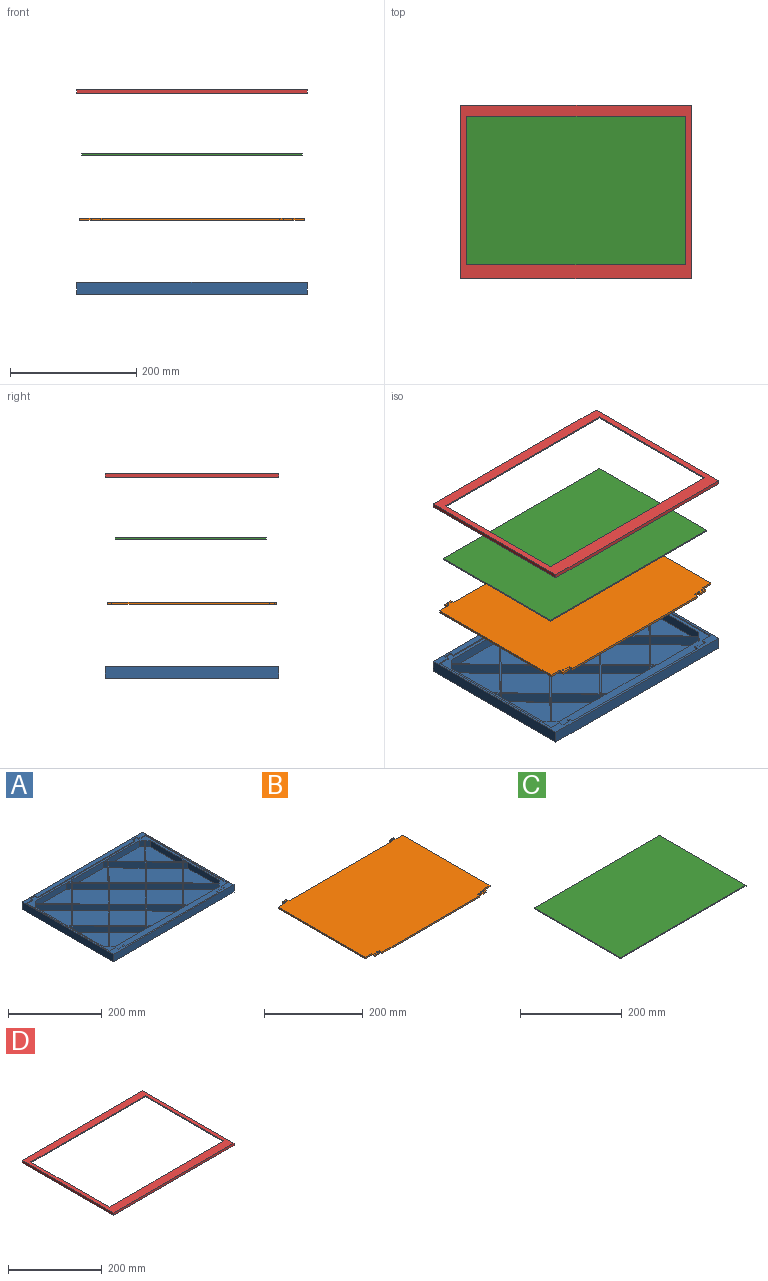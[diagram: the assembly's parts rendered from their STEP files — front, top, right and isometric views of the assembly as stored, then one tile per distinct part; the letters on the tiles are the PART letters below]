
ASSEMBLY  parts=4 mates=4
PART A: 150 faces, bbox 365x275x19 mm
  f0: plane 365x19mm, normal (0,-1,0), area 6935mm2, adj f1,f3,f4,f29
  f1: plane 275x19mm, normal (1,0,0), area 5225mm2, adj f0,f2,f4,f29
  f2: plane 365x19mm, normal (0,1,0), area 6935mm2, adj f1,f3,f4,f29
  f3: plane 275x19mm, normal (-1,0,0), area 5225mm2, adj f0,f2,f4,f29
  f4: plane 365x275mm, normal (0,0,-1), area 100375mm2, adj f0,f1,f2,f3
  f5: plane 7x2mm, normal (-1,0,0), area 14mm2, adj f6,f28,f29,f30
  f6: plane 19x2mm, normal (0,-1,0), area 38mm2, adj f5,f7,f29,f30
  f7: plane 250x2mm, normal (-1,0,0), area 500mm2, adj f6,f8,f29,f30
  f8: plane 19x2mm, normal (0,1,0), area 38mm2, adj f7,f9,f29,f30
  f9: plane 8x2mm, normal (-1,0,0), area 16mm2, adj f8,f10,f29,f30
  f10: plane 15x2mm, normal (0,1,0), area 30mm2, adj f9,f11,f29,f30
  f11: plane 4x2mm, normal (1,0,0), area 8mm2, adj f10,f12,f29,f30
  f12: plane 6x2mm, normal (0,1,0), area 12mm2, adj f11,f13,f29,f30
  f13: plane 7x2mm, normal (-1,0,0), area 14mm2, adj f12,f14,f29,f30
  f14: plane 281x2mm, normal (0,1,0), area 562mm2, adj f13,f15,f29,f30
  f15: plane 7x2mm, normal (1,0,0), area 14mm2, adj f14,f16,f29,f30
  f16: plane 3x2mm, normal (0,1,0), area 6mm2, adj f15,f17,f29,f30
  f17: plane 4x2mm, normal (-1,0,0), area 8mm2, adj f16,f18,f29,f30
  f18: plane 15x2mm, normal (0,1,0), area 30mm2, adj f17,f19,f29,f30
  f19: plane 8x2mm, normal (1,0,0), area 16mm2, adj f18,f20,f29,f30
  f20: plane 19x2mm, normal (0,1,0), area 38mm2, adj f19,f21,f29,f30
  f21: plane 250x2mm, normal (1,0,0), area 500mm2, adj f20,f22,f29,f30
  f22: plane 19x2mm, normal (0,-1,0), area 38mm2, adj f21,f23,f29,f30
  f23: plane 7x2mm, normal (1,0,0), area 14mm2, adj f22,f24,f29,f30
  f24: plane 13x2mm, normal (0,-1,0), area 26mm2, adj f23,f25,f29,f30
  f25: plane 7x2mm, normal (-1,0,0), area 14mm2, adj f24,f26,f29,f30
  f26: plane 294x2mm, normal (0,-1,0), area 588mm2, adj f25,f27,f29,f30
  f27: plane 7x2mm, normal (1,0,0), area 14mm2, adj f26,f28,f29,f30
  f28: plane 13x2mm, normal (0,-1,0), area 26mm2, adj f5,f27,f29,f30
  f29: plane 365x275mm, normal (0,0,1), area 7326mm2, adj f0,f1,f2,f3,f5,f6,f7,f8
  f30: plane 358x268mm, normal (0,0,1), area 14181.1mm2, adj f5,f6,f7,f8,f9,f10,f11,f12
  f31: plane 54.85x54.05mm, normal (0.71,-0.7,0), area 1232.1mm2, adj f30,f32,f126,f143
  f32: plane 54.85x54.05mm, normal (-0.71,-0.7,0), area 1232.1mm2, adj f30,f31,f33,f143
  f33: plane 54.85x54.05mm, normal (-0.71,0.7,0), area 1232.1mm2, adj f30,f32,f126,f143
  f34: plane 55.07x54.26mm, normal (0.71,0.7,0), area 1237mm2, adj f30,f35,f104,f142
  f35: plane 54.85x54.05mm, normal (0.71,-0.7,0), area 1232.1mm2, adj f30,f34,f36,f142
  f36: plane 55.07x54.26mm, normal (-0.71,-0.7,0), area 1237mm2, adj f30,f35,f104,f142
  f37: plane 54.85x54.05mm, normal (0.71,0.7,0), area 1232.1mm2, adj f30,f38,f105,f141
  f38: plane 55.07x54.26mm, normal (0.71,-0.7,0), area 1237mm2, adj f30,f37,f39,f141
  f39: plane 54.85x54.05mm, normal (-0.71,-0.7,0), area 1232.1mm2, adj f30,f38,f105,f141
  f40: plane 55.07x54.26mm, normal (0.71,0.7,0), area 1237mm2, adj f30,f41,f106,f140
  f41: plane 55.07x54.26mm, normal (0.71,-0.7,0), area 1237mm2, adj f30,f40,f42,f140
  f42: plane 55.07x54.26mm, normal (-0.71,-0.7,0), area 1237mm2, adj f30,f41,f106,f140
  f43: plane 55.07x54.26mm, normal (0.71,0.7,0), area 1237mm2, adj f30,f44,f107,f139
  f44: plane 54.85x54.05mm, normal (0.71,-0.7,0), area 1232.1mm2, adj f30,f43,f45,f139
  f45: plane 55.07x54.26mm, normal (-0.71,-0.7,0), area 1237mm2, adj f30,f44,f107,f139
  f46: plane 54.85x54.05mm, normal (0.71,0.7,0), area 1232.1mm2, adj f30,f47,f108,f138
  f47: plane 55.07x54.26mm, normal (0.71,-0.7,0), area 1237mm2, adj f30,f46,f48,f138
  f48: plane 54.85x54.05mm, normal (-0.71,-0.7,0), area 1232.1mm2, adj f30,f47,f108,f138
  f49: plane 54.85x54.05mm, normal (0.71,-0.7,0), area 1232.1mm2, adj f30,f50,f109,f137
  f50: plane 54.85x54.05mm, normal (-0.71,-0.7,0), area 1232.1mm2, adj f30,f49,f51,f137
  f51: plane 54.85x54.05mm, normal (-0.71,0.7,0), area 1232.1mm2, adj f30,f50,f109,f137
  f52: plane 16x7.05mm, normal (0.71,-0.7,0), area 158.5mm2, adj f30,f53,f110,f136
  f53: plane 94.2x16mm, normal (0,-1,0), area 1507.1mm2, adj f30,f52,f54,f136
  f54: plane 16x7.05mm, normal (-0.71,-0.7,0), area 158.5mm2, adj f30,f53,f55,f136
  f55: plane 54.85x54.05mm, normal (-0.71,0.7,0), area 1232.1mm2, adj f30,f54,f110,f136
  f56: plane 6x5.63mm, normal (0.71,0.7,0), area 47.4mm2, adj f30,f57,f111,f144
  f57: plane 11.09x6mm, normal (0,-1,0), area 66.6mm2, adj f30,f56,f111,f144
  f58: plane 16x7.36mm, normal (0.71,-0.7,0), area 165.2mm2, adj f30,f59,f112,f135
  f59: plane 94.03x16mm, normal (0,-1,0), area 1504.4mm2, adj f30,f58,f60,f135
  f60: plane 16x7.14mm, normal (-0.71,-0.7,0), area 160.4mm2, adj f30,f59,f61,f135
  f61: plane 55.07x54.26mm, normal (-0.71,0.7,0), area 1237mm2, adj f30,f60,f112,f135
  f62: plane 94.97x16mm, normal (1,0,0), area 1519.6mm2, adj f30,f63,f113,f134
  f63: plane 16x7.37mm, normal (0.71,-0.7,0), area 165.5mm2, adj f30,f62,f64,f134
  f64: plane 54.85x54.05mm, normal (-0.71,-0.7,0), area 1232.1mm2, adj f30,f63,f65,f134
  f65: plane 54.85x54.05mm, normal (-0.71,0.7,0), area 1232.1mm2, adj f30,f64,f113,f134
  f66: plane 11.88x6mm, normal (1,0,0), area 71.3mm2, adj f30,f67,f114,f148
  f67: plane 6x5.94mm, normal (-0.71,-0.7,0), area 50.1mm2, adj f30,f66,f114,f148
  f68: plane 94.97x16mm, normal (1,0,0), area 1519.6mm2, adj f30,f69,f115,f133
  f69: plane 16x7.37mm, normal (0.71,-0.7,0), area 165.5mm2, adj f30,f68,f70,f133
  f70: plane 54.85x54.05mm, normal (-0.71,-0.7,0), area 1232.1mm2, adj f30,f69,f71,f133
  f71: plane 54.85x54.05mm, normal (-0.71,0.7,0), area 1232.1mm2, adj f30,f70,f115,f133
  f72: plane 94.03x16mm, normal (0,1,0), area 1504.4mm2, adj f30,f73,f116,f132
  f73: plane 16x7.36mm, normal (0.71,0.7,0), area 165.2mm2, adj f30,f72,f74,f132
  f74: plane 54.85x54.05mm, normal (0.71,-0.7,0), area 1232.1mm2, adj f30,f73,f75,f132
  f75: plane 55.07x54.26mm, normal (-0.71,-0.7,0), area 1237mm2, adj f30,f74,f116,f132
  f76: plane 11.09x6mm, normal (0,1,0), area 66.6mm2, adj f30,f77,f117,f147
  f77: plane 6x5.63mm, normal (0.71,-0.7,0), area 47.4mm2, adj f30,f76,f117,f147
  f78: plane 94.2x16mm, normal (0,1,0), area 1507.1mm2, adj f30,f79,f118,f131
  f79: plane 16x7.05mm, normal (0.71,0.7,0), area 158.5mm2, adj f30,f78,f80,f131
  f80: plane 54.85x54.05mm, normal (0.71,-0.7,0), area 1232.1mm2, adj f30,f79,f81,f131
  f81: plane 54.85x54.05mm, normal (-0.71,-0.7,0), area 1232.1mm2, adj f30,f80,f118,f131
  f82: plane 11.09x6mm, normal (0,1,0), area 66.6mm2, adj f30,f83,f119,f146
  f83: plane 6x5.63mm, normal (0.71,-0.7,0), area 47.4mm2, adj f30,f82,f119,f146
  f84: plane 94.03x16mm, normal (0,1,0), area 1504.4mm2, adj f30,f85,f120,f130
  f85: plane 16x7.14mm, normal (0.71,0.7,0), area 160.4mm2, adj f30,f84,f86,f130
  f86: plane 55.07x54.26mm, normal (0.71,-0.7,0), area 1237mm2, adj f30,f85,f87,f130
  f87: plane 54.85x54.05mm, normal (-0.71,-0.7,0), area 1232.1mm2, adj f30,f86,f120,f130
  f88: plane 11.09x6mm, normal (0,-1,0), area 66.6mm2, adj f30,f89,f121,f145
  f89: plane 6x5.63mm, normal (-0.71,0.7,0), area 47.4mm2, adj f30,f88,f121,f145
  f90: plane 16x7.37mm, normal (-0.71,-0.7,0), area 165.5mm2, adj f30,f91,f122,f129
  f91: plane 94.97x16mm, normal (-1,0,0), area 1519.6mm2, adj f30,f90,f92,f129
  f92: plane 16x7.37mm, normal (-0.71,0.7,0), area 165.5mm2, adj f30,f91,f93,f129
  f93: plane 54.85x54.05mm, normal (0.71,0.7,0), area 1232.1mm2, adj f30,f92,f122,f129
  f94: plane 6x5.94mm, normal (0.71,-0.7,0), area 50.1mm2, adj f30,f95,f123,f149
  f95: plane 11.88x6mm, normal (-1,0,0), area 71.3mm2, adj f30,f94,f123,f149
  f96: plane 16x7.37mm, normal (-0.71,-0.7,0), area 165.5mm2, adj f30,f97,f124,f128
  f97: plane 94.97x16mm, normal (-1,0,0), area 1519.6mm2, adj f30,f96,f98,f128
  f98: plane 16x7.37mm, normal (-0.71,0.7,0), area 165.5mm2, adj f30,f97,f99,f128
  f99: plane 54.85x54.05mm, normal (0.71,0.7,0), area 1232.1mm2, adj f30,f98,f124,f128
  f100: plane 16x7.14mm, normal (0.71,-0.7,0), area 160.4mm2, adj f30,f101,f125,f127
  f101: plane 94.03x16mm, normal (0,-1,0), area 1504.4mm2, adj f30,f100,f102,f127
  f102: plane 16x7.36mm, normal (-0.71,-0.7,0), area 165.2mm2, adj f30,f101,f103,f127
  f103: plane 54.85x54.05mm, normal (-0.71,0.7,0), area 1232.1mm2, adj f30,f102,f125,f127
  f104: plane 54.85x54.05mm, normal (-0.71,0.7,0), area 1232.1mm2, adj f30,f34,f36,f142
  f105: plane 55.07x54.26mm, normal (-0.71,0.7,0), area 1237mm2, adj f30,f37,f39,f141
  f106: plane 55.07x54.26mm, normal (-0.71,0.7,0), area 1237mm2, adj f30,f40,f42,f140
  f107: plane 54.85x54.05mm, normal (-0.71,0.7,0), area 1232.1mm2, adj f30,f43,f45,f139
  f108: plane 55.07x54.26mm, normal (-0.71,0.7,0), area 1237mm2, adj f30,f46,f48,f138
  f109: plane 54.85x54.05mm, normal (0.71,0.7,0), area 1232.1mm2, adj f30,f49,f51,f137
  f110: plane 54.85x54.05mm, normal (0.71,0.7,0), area 1232.1mm2, adj f30,f52,f55,f136
  f111: plane 6x5.63mm, normal (-0.71,0.7,0), area 47.4mm2, adj f30,f56,f57,f144
  f112: plane 54.85x54.05mm, normal (0.71,0.7,0), area 1232.1mm2, adj f30,f58,f61,f135
  f113: plane 16x7.37mm, normal (0.71,0.7,0), area 165.5mm2, adj f30,f62,f65,f134
  f114: plane 6x5.94mm, normal (-0.71,0.7,0), area 50.1mm2, adj f30,f66,f67,f148
  f115: plane 16x7.37mm, normal (0.71,0.7,0), area 165.5mm2, adj f30,f68,f71,f133
  f116: plane 16x7.14mm, normal (-0.71,0.7,0), area 160.4mm2, adj f30,f72,f75,f132
  f117: plane 6x5.63mm, normal (-0.71,-0.7,0), area 47.4mm2, adj f30,f76,f77,f147
  f118: plane 16x7.05mm, normal (-0.71,0.7,0), area 158.5mm2, adj f30,f78,f81,f131
  f119: plane 6x5.63mm, normal (-0.71,-0.7,0), area 47.4mm2, adj f30,f82,f83,f146
  f120: plane 16x7.36mm, normal (-0.71,0.7,0), area 165.2mm2, adj f30,f84,f87,f130
  f121: plane 6x5.63mm, normal (0.71,0.7,0), area 47.4mm2, adj f30,f88,f89,f145
  f122: plane 54.85x54.05mm, normal (0.71,-0.7,0), area 1232.1mm2, adj f30,f90,f93,f129
  f123: plane 6x5.94mm, normal (0.71,0.7,0), area 50.1mm2, adj f30,f94,f95,f149
  f124: plane 54.85x54.05mm, normal (0.71,-0.7,0), area 1232.1mm2, adj f30,f96,f99,f128
  f125: plane 55.07x54.26mm, normal (0.71,0.7,0), area 1237mm2, adj f30,f100,f103,f127
  f126: plane 54.85x54.05mm, normal (0.71,0.7,0), area 1232.1mm2, adj f30,f31,f33,f143
  f127: plane 108.31x62.21mm, normal (0,0,1), area 3709.7mm2, adj f100,f101,f102,f103,f125
  f128: plane 109.71x61.31mm, normal (0,0,1), area 3707.7mm2, adj f96,f97,f98,f99,f124
  f129: plane 109.71x61.31mm, normal (0,0,1), area 3707.7mm2, adj f90,f91,f92,f93,f122
  f130: plane 108.31x62.21mm, normal (0,0,1), area 3709.7mm2, adj f84,f85,f86,f87,f120
  f131: plane 108.1x61.91mm, normal (0,0,1), area 3678.4mm2, adj f78,f79,f80,f81,f118
  f132: plane 108.31x62.21mm, normal (0,0,1), area 3709.7mm2, adj f72,f73,f74,f75,f116
  f133: plane 109.71x61.31mm, normal (0,0,1), area 3707.7mm2, adj f68,f69,f70,f71,f115
  f134: plane 109.71x61.31mm, normal (0,0,1), area 3707.7mm2, adj f62,f63,f64,f65,f113
  f135: plane 108.31x62.21mm, normal (0,0,1), area 3709.7mm2, adj f58,f59,f60,f61,f112
  f136: plane 108.1x61.91mm, normal (0,0,1), area 3678.4mm2, adj f52,f53,f54,f55,f110
  f137: plane 109.71x108.1mm, normal (0,0,1), area 5929.6mm2, adj f49,f50,f51,f109
  f138: plane 109.92x108.31mm, normal (0,0,1), area 5952.9mm2, adj f46,f47,f48,f108
  f139: plane 109.92x108.31mm, normal (0,0,1), area 5952.9mm2, adj f43,f44,f45,f107
  f140: plane 110.14x108.52mm, normal (0,0,1), area 5976.2mm2, adj f40,f41,f42,f106
  f141: plane 109.92x108.31mm, normal (0,0,1), area 5952.9mm2, adj f37,f38,f39,f105
  f142: plane 109.92x108.31mm, normal (0,0,1), area 5952.9mm2, adj f34,f35,f36,f104
  f143: plane 109.71x108.1mm, normal (0,0,1), area 5929.6mm2, adj f31,f32,f33,f126
  f144: plane 11.09x5.63mm, normal (0,0,1), area 31.2mm2, adj f56,f57,f111
  f145: plane 11.09x5.63mm, normal (0,0,1), area 31.2mm2, adj f88,f89,f121
  f146: plane 11.09x5.63mm, normal (0,0,1), area 31.2mm2, adj f82,f83,f119
  f147: plane 11.09x5.63mm, normal (0,0,1), area 31.2mm2, adj f76,f77,f117
  f148: plane 11.88x5.86mm, normal (0,0,1), area 34.8mm2, adj f66,f67,f114
  f149: plane 11.88x5.86mm, normal (0,0,1), area 34.8mm2, adj f94,f95,f123
PART B: 34 faces, bbox 358x268x3.5 mm
  f0: plane 7x3.5mm, normal (1,0,0), area 24.5mm2, adj f1,f30,f32,f33
  f1: plane 6x3.5mm, normal (0,-1,0), area 21mm2, adj f0,f2,f32,f33
  f2: plane 4x3.5mm, normal (-1,0,0), area 14mm2, adj f1,f3,f32,f33
  f3: plane 15x3.5mm, normal (0,-1,0), area 52.5mm2, adj f2,f4,f32,f33
  f4: plane 8x3.5mm, normal (1,0,0), area 28mm2, adj f3,f5,f32,f33
  f5: plane 19x3.5mm, normal (0,-1,0), area 66.5mm2, adj f4,f6,f32,f33
  f6: plane 250x3.5mm, normal (1,0,0), area 875mm2, adj f5,f7,f32,f33
  f7: plane 19x3.5mm, normal (0,1,0), area 66.5mm2, adj f6,f8,f32,f33
  f8: plane 7x3.5mm, normal (1,0,0), area 24.5mm2, adj f7,f9,f32,f33
  f9: plane 13x3.5mm, normal (0,1,0), area 45.5mm2, adj f8,f10,f32,f33
  f10: plane 7x3.5mm, normal (-1,0,0), area 24.5mm2, adj f9,f11,f32,f33
  f11: plane 294x3.5mm, normal (0,1,0), area 1029mm2, adj f10,f12,f32,f33
  f12: plane 7x3.5mm, normal (1,0,0), area 24.5mm2, adj f11,f13,f32,f33
  f13: plane 13x3.5mm, normal (0,1,0), area 45.5mm2, adj f12,f14,f32,f33
  f14: plane 7x3.5mm, normal (-1,0,0), area 24.5mm2, adj f13,f15,f32,f33
  f15: plane 19x3.5mm, normal (0,1,0), area 66.5mm2, adj f14,f16,f32,f33
  f16: plane 250x3.5mm, normal (-1,0,0), area 875mm2, adj f15,f17,f32,f33
  f17: plane 19x3.5mm, normal (0,-1,0), area 66.5mm2, adj f16,f18,f32,f33
  f18: plane 8x3.5mm, normal (-1,0,0), area 28mm2, adj f17,f19,f32,f33
  f19: plane 15x3.5mm, normal (0,-1,0), area 52.5mm2, adj f18,f20,f32,f33
  f20: plane 4x3.5mm, normal (1,0,0), area 14mm2, adj f19,f21,f32,f33
  f21: plane 3.5x3mm, normal (0,-1,0), area 10.5mm2, adj f20,f22,f32,f33
  f22: plane 7x3.5mm, normal (-1,0,0), area 24.5mm2, adj f21,f30,f32,f33
  f23: cylinder r=1mm len=3.5mm, axis (0,0,-1), area 22mm2, adj f32,f33
  f24: cylinder r=1mm len=3.5mm, axis (0,0,-1), area 22mm2, adj f32,f33
  f25: cylinder r=1mm len=3.5mm, axis (0,0,-1), area 22mm2, adj f32,f33
  f26: cylinder r=1mm len=3.5mm, axis (0,0,-1), area 22mm2, adj f32,f33
  f27: cylinder r=1mm len=3.5mm, axis (0,0,-1), area 22mm2, adj f32,f33
  f28: cylinder r=1mm len=3.5mm, axis (0,0,-1), area 22mm2, adj f32,f33
  f29: cylinder r=1mm len=3.5mm, axis (0,0,-1), area 22mm2, adj f32,f33
  f30: plane 281x3.5mm, normal (0,-1,0), area 983.5mm2, adj f0,f22,f32,f33
  f31: cylinder r=1mm len=3.5mm, axis (0,0,-1), area 22mm2, adj f32,f33
  f32: plane 358x268mm, normal (0,0,1), area 93023.9mm2, adj f0,f1,f2,f3,f4,f5,f6,f7
  f33: plane 358x268mm, normal (0,0,-1), area 93023.9mm2, adj f0,f1,f2,f3,f4,f5,f6,f7
PART C: 6 faces, bbox 350x240x2 mm
  f0: plane 240x2mm, normal (1,0,0), area 480mm2, adj f1,f3,f4,f5
  f1: plane 350x2mm, normal (0,1,0), area 700mm2, adj f0,f2,f4,f5
  f2: plane 240x2mm, normal (-1,0,0), area 480mm2, adj f1,f3,f4,f5
  f3: plane 350x2mm, normal (0,-1,0), area 700mm2, adj f0,f2,f4,f5
  f4: plane 350x240mm, normal (0,0,1), area 84000mm2, adj f0,f1,f2,f3
  f5: plane 350x240mm, normal (0,0,-1), area 84000mm2, adj f0,f1,f2,f3
PART D: 40 faces, bbox 365x275x6 mm
  f0: plane 275x6mm, normal (-1,0,0), area 1650mm2, adj f1,f27,f28,f38
  f1: plane 365x6mm, normal (0,-1,0), area 2190mm2, adj f0,f2,f28,f38
  f2: plane 275x6mm, normal (1,0,0), area 1650mm2, adj f1,f27,f28,f38
  f3: plane 7x2mm, normal (-1,0,0), area 14mm2, adj f4,f26,f28,f33
  f4: plane 19x2mm, normal (0,-1,0), area 38mm2, adj f3,f5,f28,f33
  f5: plane 250x2mm, normal (-1,0,0), area 500mm2, adj f4,f6,f28,f33
  f6: plane 19x2mm, normal (0,1,0), area 38mm2, adj f5,f7,f28,f33
  f7: plane 8x2mm, normal (-1,0,0), area 16mm2, adj f6,f8,f28,f33
  f8: plane 15x2mm, normal (0,1,0), area 30mm2, adj f7,f9,f28,f33
  f9: plane 4x2mm, normal (1,0,0), area 8mm2, adj f8,f10,f28,f33
  f10: plane 6x2mm, normal (0,1,0), area 12mm2, adj f9,f11,f28,f33
  f11: plane 7x2mm, normal (-1,0,0), area 14mm2, adj f10,f12,f28,f33
  f12: plane 281x2mm, normal (0,1,0), area 562mm2, adj f11,f13,f28,f33
  f13: plane 7x2mm, normal (1,0,0), area 14mm2, adj f12,f14,f28,f33
  f14: plane 3x2mm, normal (0,1,0), area 6mm2, adj f13,f15,f28,f33
  f15: plane 4x2mm, normal (-1,0,0), area 8mm2, adj f14,f16,f28,f33
  f16: plane 15x2mm, normal (0,1,0), area 30mm2, adj f15,f17,f28,f33
  f17: plane 8x2mm, normal (1,0,0), area 16mm2, adj f16,f18,f28,f33
  f18: plane 19x2mm, normal (0,1,0), area 38mm2, adj f17,f19,f28,f33
  f19: plane 250x2mm, normal (1,0,0), area 500mm2, adj f18,f20,f28,f33
  f20: plane 19x2mm, normal (0,-1,0), area 38mm2, adj f19,f21,f28,f33
  f21: plane 7x2mm, normal (1,0,0), area 14mm2, adj f20,f22,f28,f33
  f22: plane 13x2mm, normal (0,-1,0), area 26mm2, adj f21,f23,f28,f33
  f23: plane 7x2mm, normal (-1,0,0), area 14mm2, adj f22,f24,f28,f33
  f24: plane 294x2mm, normal (0,-1,0), area 588mm2, adj f23,f25,f28,f33
  f25: plane 7x2mm, normal (1,0,0), area 14mm2, adj f24,f26,f28,f33
  f26: plane 13x2mm, normal (0,-1,0), area 26mm2, adj f3,f25,f28,f33
  f27: plane 365x6mm, normal (0,1,0), area 2190mm2, adj f0,f2,f28,f38
  f28: plane 365x275mm, normal (0,0,-1), area 7326mm2, adj f0,f1,f2,f3,f4,f5,f6,f7
  f29: plane 350x2mm, normal (0,-1,0), area 700mm2, adj f30,f32,f33,f39
  f30: plane 240x2mm, normal (-1,0,0), area 480mm2, adj f29,f31,f33,f39
  f31: plane 350x2mm, normal (0,1,0), area 700mm2, adj f30,f32,f33,f39
  f32: plane 240x2mm, normal (1,0,0), area 480mm2, adj f29,f31,f33,f39
  f33: plane 358x268mm, normal (0,0,-1), area 9049mm2, adj f3,f4,f5,f6,f7,f8,f9,f10
  f34: plane 346x2mm, normal (0,-1,0), area 692mm2, adj f35,f37,f38,f39
  f35: plane 236x2mm, normal (-1,0,0), area 472mm2, adj f34,f36,f38,f39
  f36: plane 346x2mm, normal (0,1,0), area 692mm2, adj f35,f37,f38,f39
  f37: plane 236x2mm, normal (1,0,0), area 472mm2, adj f34,f36,f38,f39
  f38: plane 365x275mm, normal (0,0,1), area 18719mm2, adj f0,f1,f2,f27,f34,f35,f36,f37
  f39: plane 350x240mm, normal (0,0,-1), area 2344mm2, adj f29,f30,f31,f32,f34,f35,f36,f37
PLACE A rot(axis=(0,0,1),0deg) t=(-711.1,-341.98,-457.03)mm
PLACE B rot(axis=(0,0,1),0deg) t=(-711.1,-341.98,-340.53)mm
PLACE C t=(-711.1,-341.98,-237.03)mm
PLACE D t=(-711.1,-341.98,-157.03)mm
MATE slider C.f4 <-> D.f39  axis (0,0,1) through (-536.1,-221.98,-235.03)mm
MATE slider D.f28 <-> A.f29  axis (0,0,-1) through (-551.1,-216.98,-139.03)mm
MATE slider A.f29 <-> D.f28  axis (0,0,1) through (-528.6,-206.48,-439.03)mm
MATE slider B.f32 <-> D.f33  axis (0,0,1) through (-551.1,-216.98,-337.03)mm
